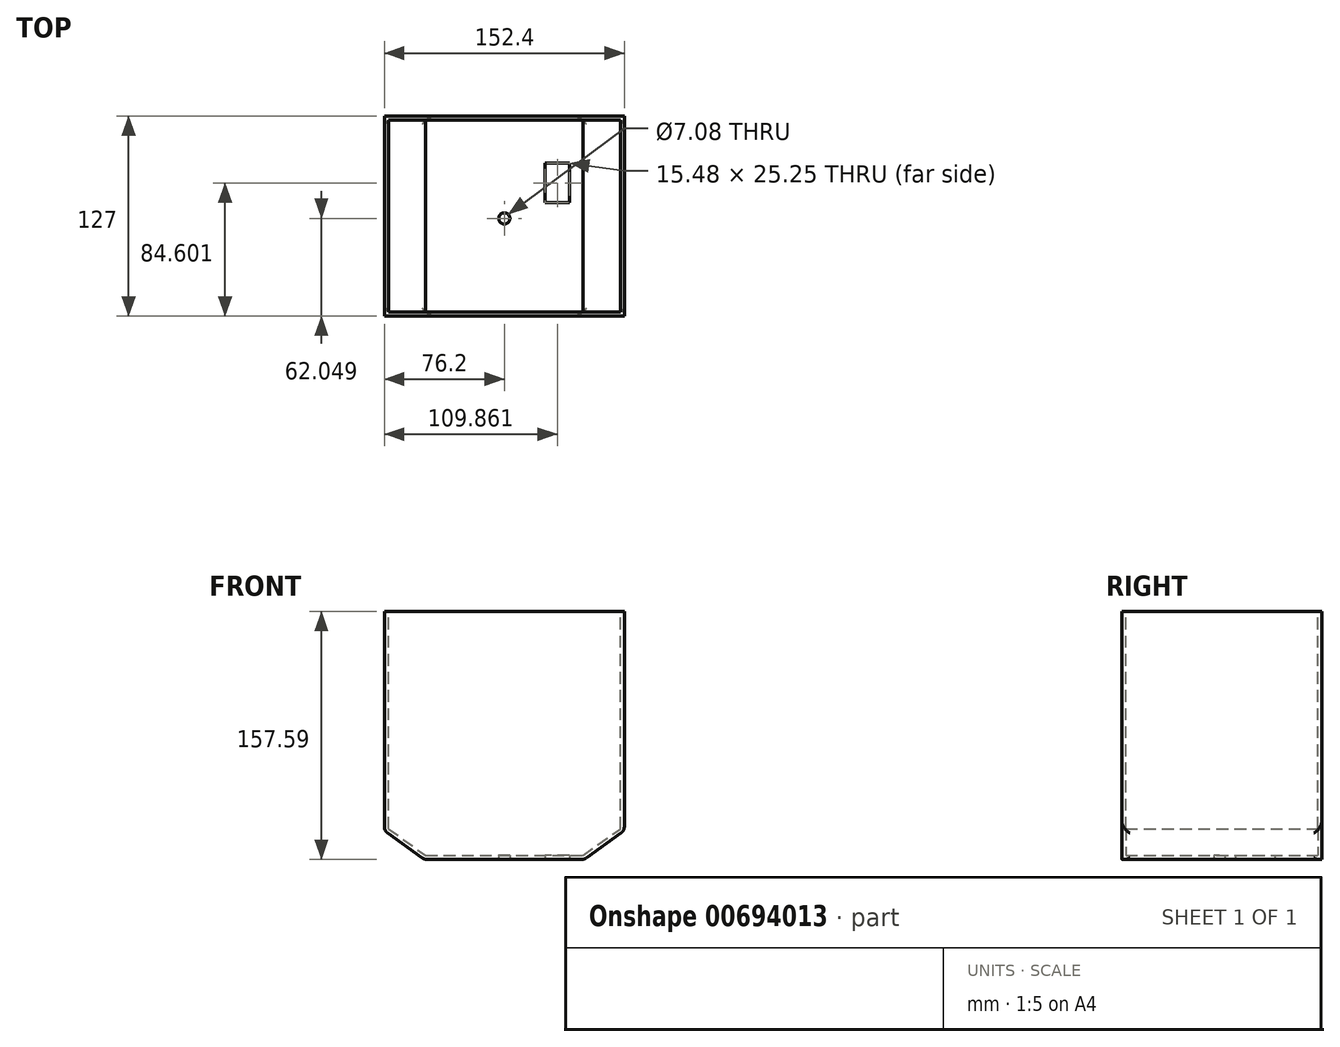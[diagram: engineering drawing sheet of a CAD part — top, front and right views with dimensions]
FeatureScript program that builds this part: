
annotation { "Feature Type Name" : "Feature", "Feature Type Description" : "" }
export const myFeature = defineFeature(function(context is Context, id is Id, definition is map)
    precondition{}
    {
        {
            var Q0;
            Q0=qCreatedBy(makeId("Front.planeOp"),FACE);
            var sketch = newSketch(context, id + "F0", { "sketchPlane" : qUnion([Q0])});
            skLineSegment(sketch, "E0.bottom", {"start": v(-76.2, -69.69) * mm, "end": v(76.2, -69.69) * mm});
            skLineSegment(sketch, "E0.top", {"start": v(-76.2, 69.69) * mm, "end": v(76.2, 69.69) * mm});
            skLineSegment(sketch, "E0.left", {"start": v(-76.2, -69.69) * mm, "end": v(-76.2, 69.69) * mm});
            skLineSegment(sketch, "E0.right", {"start": v(76.2, -69.69) * mm, "end": v(76.2, 69.69) * mm});
            skPoint(sketch, "E0.middle", {"position": v(0, 0) * mm});
            skLineSegment(sketch, "E1.bottom", {"start": v(-50.8, -87.9) * mm, "end": v(50.8, -87.9) * mm});
            skLineSegment(sketch, "E1.top", {"start": v(-50.8, -51.47) * mm, "end": v(50.8, -51.47) * mm});
            skLineSegment(sketch, "E1.left", {"start": v(-50.8, -87.9) * mm, "end": v(-50.8, -51.47) * mm});
            skLineSegment(sketch, "E1.right", {"start": v(50.8, -87.9) * mm, "end": v(50.8, -51.47) * mm});
            skPoint(sketch, "E1.middle", {"position": v(0, -69.69) * mm});
            skLineSegment(sketch, "E2", {"start": v(-76.2, -69.69) * mm, "end": v(-50.8, -87.9) * mm});
            skLineSegment(sketch, "E3", {"start": v(50.8, -87.9) * mm, "end": v(76.2, -69.69) * mm});
            skSolve(sketch);
        }
        {
            var Q0;
            {var subQ5=sQuery(id+"F0.wireOp",EDGE,"E1.top");Q0=makeQuery(id+"F0.imprint","IMPRINT",FACE,{"disambiguationData":[TD([[makeQuery(id+"F0.imprint","IMPRINT",EDGE,{"derivedFrom":subQ5}),-1.0]])]});}
            var Q1;
            {var subQ0=sQuery(id+"F0.wireOp",EDGE,"E2");Q1=makeQuery(id+"F0.imprint","IMPRINT",FACE,{"disambiguationData":[TD([[makeQuery(id+"F0.imprint","IMPRINT",EDGE,{"derivedFrom":subQ0}),1.0]])]});}
            var Q2;
            Q2=makeQuery(id+"F0.imprint","IMPRINT",FACE,{"disambiguationData":[TD([[makeQuery(id+"F0.imprint","IMPRINT",EDGE,{"derivedFrom":sQuery(id+"F0.wireOp",EDGE,"E0.top")}),-1.0]])]});
            var Q3;
            {var subQ0=sQuery(id+"F0.wireOp",EDGE,"E3");Q3=makeQuery(id+"F0.imprint","IMPRINT",FACE,{"disambiguationData":[TD([[makeQuery(id+"F0.imprint","IMPRINT",EDGE,{"derivedFrom":subQ0}),1.0]])]});}
            var Q4;
            {var subQ5=sQuery(id+"F0.wireOp",EDGE,"E1.bottom");Q4=makeQuery(id+"F0.imprint","IMPRINT",FACE,{"disambiguationData":[TD([[makeQuery(id+"F0.imprint","IMPRINT",EDGE,{"derivedFrom":subQ5}),1.0]])]});}
            extrude(context, id + "F1", {"entities" : qUnion([Q0, Q1, Q2, Q3, Q4]), "depth" : 127 * mm, "offsetDistance" : 25.4 * mm});
        }
        {
            var Q0;
            {var subQ0=sQuery(id+"F0.wireOp",EDGE,"E3");Q0=makeQuery(id+"F0.imprint","IMPRINT",FACE,{"disambiguationData":[TD([[makeQuery(id+"F0.imprint","IMPRINT",EDGE,{"derivedFrom":subQ0}),1.0]])]});}
            var Q1;
            Q1=makeQuery(id+"F0.imprint","IMPRINT",FACE,{"disambiguationData":[TD([[makeQuery(id+"F0.imprint","IMPRINT",EDGE,{"derivedFrom":sQuery(id+"F0.wireOp",EDGE,"E0.top")}),-1.0]])]});
            var Q2;
            {var subQ5=sQuery(id+"F0.wireOp",EDGE,"E1.bottom");Q2=makeQuery(id+"F0.imprint","IMPRINT",FACE,{"disambiguationData":[TD([[makeQuery(id+"F0.imprint","IMPRINT",EDGE,{"derivedFrom":subQ5}),1.0]])]});}
            var Q3;
            {var subQ5=sQuery(id+"F0.wireOp",EDGE,"E1.top");Q3=makeQuery(id+"F0.imprint","IMPRINT",FACE,{"disambiguationData":[TD([[makeQuery(id+"F0.imprint","IMPRINT",EDGE,{"derivedFrom":subQ5}),-1.0]])]});}
            var Q4;
            Q4 = qSketchRegion(id + "F0", true);
            var Q5;
            {var subQ0=sQuery(id+"F0.wireOp",EDGE,"E2");Q5=makeQuery(id+"F0.imprint","IMPRINT",FACE,{"disambiguationData":[TD([[makeQuery(id+"F0.imprint","IMPRINT",EDGE,{"derivedFrom":subQ0}),1.0]])]});}
            extrude(context, id + "F2", {"entities" : qUnion([Q0, Q1, Q2, Q3, Q4, Q5]), "operationType" : NewBodyOperationType.ADD, "depth" : 127 * mm, "offsetDistance" : 25.4 * mm});
        }
        {
            var Q0;
            Q0=makeQuery(id+"F1.opExtrude","SWEPT_FACE",FACE,{"disambiguationData":[OSD([sQuery(id+"F0.wireOp",EDGE,"E0.top")])]});
            shell(context, id + "F3", {"entities" : qUnion([Q0]), "thickness" : 2.54 * mm});
        }
        {
            var Q0;
            Q0=makeQuery(id+"F1.opExtrude","SWEPT_FACE",FACE,{"disambiguationData":[OSD([sQuery(id+"F0.wireOp",EDGE,"E1.bottom")])]});
            var sketch = newSketch(context, id + "F4", { "sketchPlane" : qUnion([Q0])});
            skLineSegment(sketch, "E4.bottom", {"start": v(25.92, 29.78) * mm, "end": v(41.4, 29.78) * mm});
            skLineSegment(sketch, "E4.top", {"start": v(25.92, 55.02) * mm, "end": v(41.4, 55.02) * mm});
            skLineSegment(sketch, "E4.left", {"start": v(25.92, 29.78) * mm, "end": v(25.92, 55.02) * mm});
            skLineSegment(sketch, "E4.right", {"start": v(41.4, 29.78) * mm, "end": v(41.4, 55.02) * mm});
            skPoint(sketch, "E4.middle", {"position": v(33.66, 42.4) * mm});
            skSolve(sketch);
        }
        {
            var Q0;
            Q0=makeQuery(id+"F4.imprint","IMPRINT",FACE,{"disambiguationData":[TD([[makeQuery(id+"F4.imprint","IMPRINT",EDGE,{"derivedFrom":sQuery(id+"F4.wireOp",EDGE,"E4.bottom")}),1.0]])]});
            extrude(context, id + "F5", {"entities" : qUnion([Q0]), "operationType" : NewBodyOperationType.REMOVE, "oppositeDirection" : true, "depth" : 25.4 * mm, "offsetDistance" : 25.4 * mm});
        }
        {
            var Q0;
            Q0=makeQuery(id+"F1.opExtrude","SWEPT_FACE",FACE,{"disambiguationData":[OSD([sQuery(id+"F0.wireOp",EDGE,"E1.bottom")])]});
            var sketch = newSketch(context, id + "F6", { "sketchPlane" : qUnion([Q0])});
            skCircle(sketch, "E5", {"center": v(0, 64.95) * mm, "radius": 3.54 * mm});
            skSolve(sketch);
        }
        {
            var Q0;
            Q0 = qSketchRegion(id + "F6", true);
            extrude(context, id + "F7", {"entities" : qUnion([Q0]), "operationType" : NewBodyOperationType.REMOVE, "oppositeDirection" : true, "depth" : 25.4 * mm, "offsetDistance" : 25.4 * mm});
        }
        {
            var Q0;
            Q0=makeQuery(id+"F1.opExtrude","SWEPT_FACE",FACE,{"disambiguationData":[OSD([sQuery(id+"F0.wireOp",EDGE,"E3")])]});
            fillet(context, id + "F8", {"entities" : qUnion([Q0]), "radius" : 5.08 * mm, "tangentPropagation" : true, "allowEdgeOverflow" : false});
        }
        {
            var Q0;
            Q0=makeQuery(id+"F1.opExtrude","SWEPT_FACE",FACE,{"disambiguationData":[OSD([sQuery(id+"F0.wireOp",EDGE,"E2")])]});
            fillet(context, id + "F9", {"entities" : qUnion([Q0]), "radius" : 5.08 * mm, "tangentPropagation" : true, "allowEdgeOverflow" : false});
        }
    });
